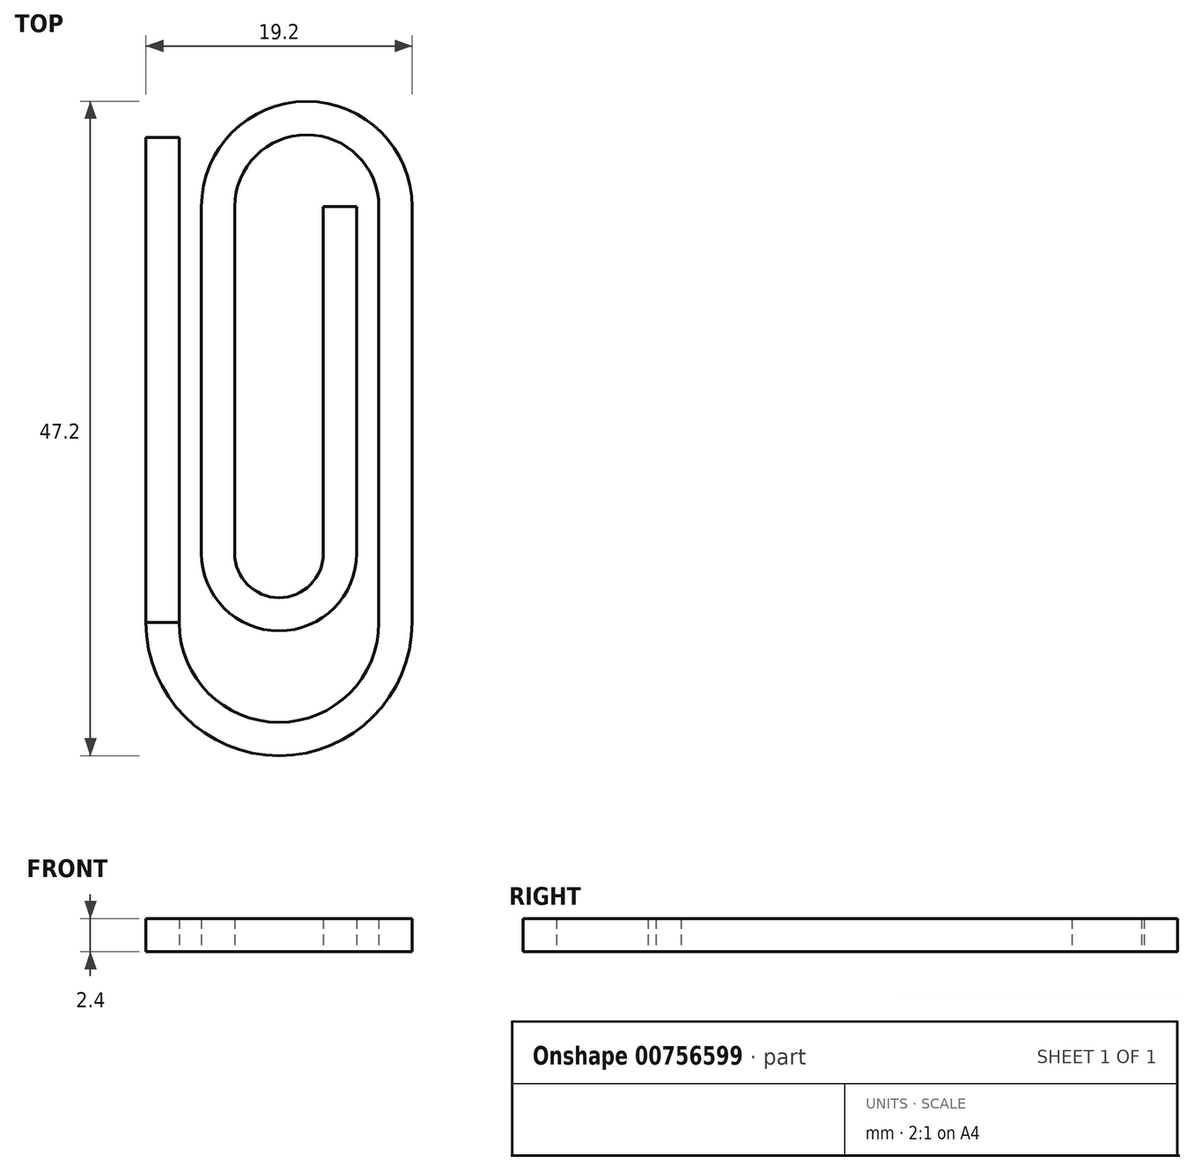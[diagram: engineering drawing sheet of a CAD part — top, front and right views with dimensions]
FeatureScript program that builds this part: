
annotation { "Feature Type Name" : "Feature", "Feature Type Description" : "" }
export const myFeature = defineFeature(function(context is Context, id is Id, definition is map)
    precondition{}
    {
        {
            var Q0;
            Q0=qCreatedBy(makeId("Front.planeOp"),FACE);
            var sketch = newSketch(context, id + "F0", { "sketchPlane" : qUnion([Q0])});
            skLineSegment(sketch, "E0.bottom", {"start": v(-31.47, 2.4) * mm, "end": v(-29.07, 2.4) * mm});
            skLineSegment(sketch, "E0.top", {"start": v(-31.47, 0) * mm, "end": v(-29.07, 0) * mm});
            skLineSegment(sketch, "E0.left", {"start": v(-31.47, 2.4) * mm, "end": v(-31.47, 0) * mm});
            skLineSegment(sketch, "E0.right", {"start": v(-29.07, 2.4) * mm, "end": v(-29.07, 0) * mm});
            skSolve(sketch);
        }
        {
            var Q0;
            Q0 = qSketchRegion(id + "F0", true);
            extrude(context, id + "F1", {"entities" : qUnion([Q0]), "depth" : 35 * mm, "offsetDistance" : 25 * mm});
        }
        {
            var Q0;
            Q0=makeQuery(id+"F1.opExtrude","CAP_FACE",FACE,{"disambiguationData":[OSD([sQuery(id+"F0.wireOp",EDGE,"E0.bottom"),sQuery(id+"F0.wireOp",EDGE,"E0.top"),sQuery(id+"F0.wireOp",EDGE,"E0.left"),sQuery(id+"F0.wireOp",EDGE,"E0.right")])],"isStart":false});
            var sketch = newSketch(context, id + "F2", { "sketchPlane" : qUnion([Q0])});
            skLineSegment(sketch, "E1", {"start": v(-31.47, 1.2) * mm, "end": v(-21.87, 1.2) * mm});
            skLineSegment(sketch, "E2", {"start": v(-21.87, 1.2) * mm, "end": v(-21.87, 0) * mm});
            skSolve(sketch);
        }
        {
            var Q0;
            {var subQ5=makeQuery(id+"F1.opExtrude","CAP_EDGE",EDGE,{"disambiguationData":[OSD([sQuery(id+"F0.wireOp",EDGE,"E0.bottom")])],"isStart":false});Q0=makeQuery(id+"F2.imprint","IMPRINT",FACE,{"disambiguationData":[TD([[makeQuery(id+"F2.imprint","IMPRINT",EDGE,{"derivedFrom":subQ5}),-1.0]])]});}
            var Q1;
            {var subQ5=makeQuery(id+"F1.opExtrude","CAP_EDGE",EDGE,{"disambiguationData":[OSD([sQuery(id+"F0.wireOp",EDGE,"E0.top")])],"isStart":false});Q1=makeQuery(id+"F2.imprint","IMPRINT",FACE,{"disambiguationData":[TD([[makeQuery(id+"F2.imprint","IMPRINT",EDGE,{"derivedFrom":subQ5}),1.0]])]});}
            var Q2;
            Q2=sQuery(id+"F2.wireOp",EDGE,"E2");
            revolve(context, id + "F3", {"surfaceOperationType" : NewSurfaceOperationType.NEW, "entities" : qUnion([Q0, Q1]), "axis" : qUnion([Q2]), "revolveType" : RevolveType.ONE_DIRECTION, "oppositeDirection" : true, "angle" : 180 * degree});
        }
        {
            var Q0;
            Q0=makeQuery(id+"F3.opRevolve","CAP_FACE",FACE,{"disambiguationData":[OSD([sQuery(id+"F0.wireOp",EDGE,"E0.bottom"),sQuery(id+"F0.wireOp",EDGE,"E0.top"),sQuery(id+"F0.wireOp",EDGE,"E0.left"),sQuery(id+"F0.wireOp",EDGE,"E0.right")])],"isStart":false});
            extrude(context, id + "F4", {"entities" : qUnion([Q0]), "operationType" : NewBodyOperationType.ADD, "depth" : 30 * mm, "offsetDistance" : 25 * mm});
        }
        {
            var Q0;
            Q0=makeQuery(id+"F4.opExtrude","CAP_FACE",FACE,{"disambiguationData":[OSD([sQuery(id+"F0.wireOp",EDGE,"E0.bottom"),sQuery(id+"F0.wireOp",EDGE,"E0.top"),sQuery(id+"F0.wireOp",EDGE,"E0.left"),sQuery(id+"F0.wireOp",EDGE,"E0.right")])],"isStart":false});
            var sketch = newSketch(context, id + "F5", { "sketchPlane" : qUnion([Q0])});
            skLineSegment(sketch, "E3", {"start": v(12.27, 1.2) * mm, "end": v(19.87, 1.2) * mm});
            skPoint(sketch, "E3.endSnap0", {"position": v(14.67, 1.2) * mm});
            skLineSegment(sketch, "E4", {"start": v(19.87, 1.2) * mm, "end": v(19.87, 0) * mm});
            skSolve(sketch);
        }
        {
            var Q0;
            {var subQ5=makeQuery(id+"F4.opExtrude","CAP_EDGE",EDGE,{"disambiguationData":[OSD([sQuery(id+"F0.wireOp",EDGE,"E0.bottom")])],"isStart":false});Q0=makeQuery(id+"F5.imprint","IMPRINT",FACE,{"disambiguationData":[TD([[makeQuery(id+"F5.imprint","IMPRINT",EDGE,{"derivedFrom":subQ5}),-1.0]])]});}
            var Q1;
            {var subQ5=makeQuery(id+"F4.opExtrude","CAP_EDGE",EDGE,{"disambiguationData":[OSD([sQuery(id+"F0.wireOp",EDGE,"E0.top")])],"isStart":false});Q1=makeQuery(id+"F5.imprint","IMPRINT",FACE,{"disambiguationData":[TD([[makeQuery(id+"F5.imprint","IMPRINT",EDGE,{"derivedFrom":subQ5}),1.0]])]});}
            var Q2;
            Q2=sQuery(id+"F5.wireOp",EDGE,"E4");
            revolve(context, id + "F6", {"operationType" : NewBodyOperationType.ADD, "surfaceOperationType" : NewSurfaceOperationType.NEW, "entities" : qUnion([Q0, Q1]), "axis" : qUnion([Q2]), "revolveType" : RevolveType.ONE_DIRECTION, "oppositeDirection" : true, "angle" : 180 * degree});
        }
        {
            var Q0;
            Q0=makeQuery(id+"F6.opRevolve","CAP_FACE",FACE,{"disambiguationData":[OSD([sQuery(id+"F0.wireOp",EDGE,"E0.bottom"),sQuery(id+"F0.wireOp",EDGE,"E0.top"),sQuery(id+"F0.wireOp",EDGE,"E0.left"),sQuery(id+"F0.wireOp",EDGE,"E0.right")])],"isStart":false});
            extrude(context, id + "F7", {"entities" : qUnion([Q0]), "operationType" : NewBodyOperationType.ADD, "depth" : 25 * mm, "offsetDistance" : 25 * mm});
        }
        {
            var Q0;
            Q0=makeQuery(id+"F7.opExtrude","CAP_FACE",FACE,{"disambiguationData":[OSD([sQuery(id+"F0.wireOp",EDGE,"E0.bottom"),sQuery(id+"F0.wireOp",EDGE,"E0.top"),sQuery(id+"F0.wireOp",EDGE,"E0.left"),sQuery(id+"F0.wireOp",EDGE,"E0.right")])],"isStart":false});
            var sketch = newSketch(context, id + "F8", { "sketchPlane" : qUnion([Q0])});
            skLineSegment(sketch, "E5", {"start": v(-27.47, 2.4) * mm, "end": v(-21.87, 2.4) * mm});
            skLineSegment(sketch, "E6", {"start": v(-21.87, 2.4) * mm, "end": v(-21.87, 1.25) * mm});
            skSolve(sketch);
        }
        {
            var Q0;
            Q0=makeQuery(id+"F8.imprint","IMPRINT",FACE,{"disambiguationData":[TD([[makeQuery(id+"F8.imprint","IMPRINT",EDGE,{"derivedFrom":makeQuery(id+"F7.opExtrude","CAP_EDGE",EDGE,{"disambiguationData":[OSD([sQuery(id+"F0.wireOp",EDGE,"E0.top")])],"isStart":false})}),1.0]])]});
            var Q1;
            Q1=sQuery(id+"F8.wireOp",EDGE,"E6");
            revolve(context, id + "F9", {"operationType" : NewBodyOperationType.ADD, "surfaceOperationType" : NewSurfaceOperationType.NEW, "entities" : qUnion([Q0]), "axis" : qUnion([Q1]), "revolveType" : RevolveType.ONE_DIRECTION, "oppositeDirection" : true, "angle" : 180 * degree});
        }
        {
            var Q0;
            Q0=makeQuery(id+"F9.opRevolve","CAP_FACE",FACE,{"disambiguationData":[OSD([sQuery(id+"F0.wireOp",EDGE,"E0.top"),sQuery(id+"F0.wireOp",EDGE,"E0.left"),sQuery(id+"F0.wireOp",EDGE,"E0.right"),sQuery(id+"F8.wireOp",EDGE,"E5")])],"isStart":false});
            extrude(context, id + "F10", {"entities" : qUnion([Q0]), "operationType" : NewBodyOperationType.ADD, "depth" : 25 * mm, "offsetDistance" : 25 * mm});
        }
    });
